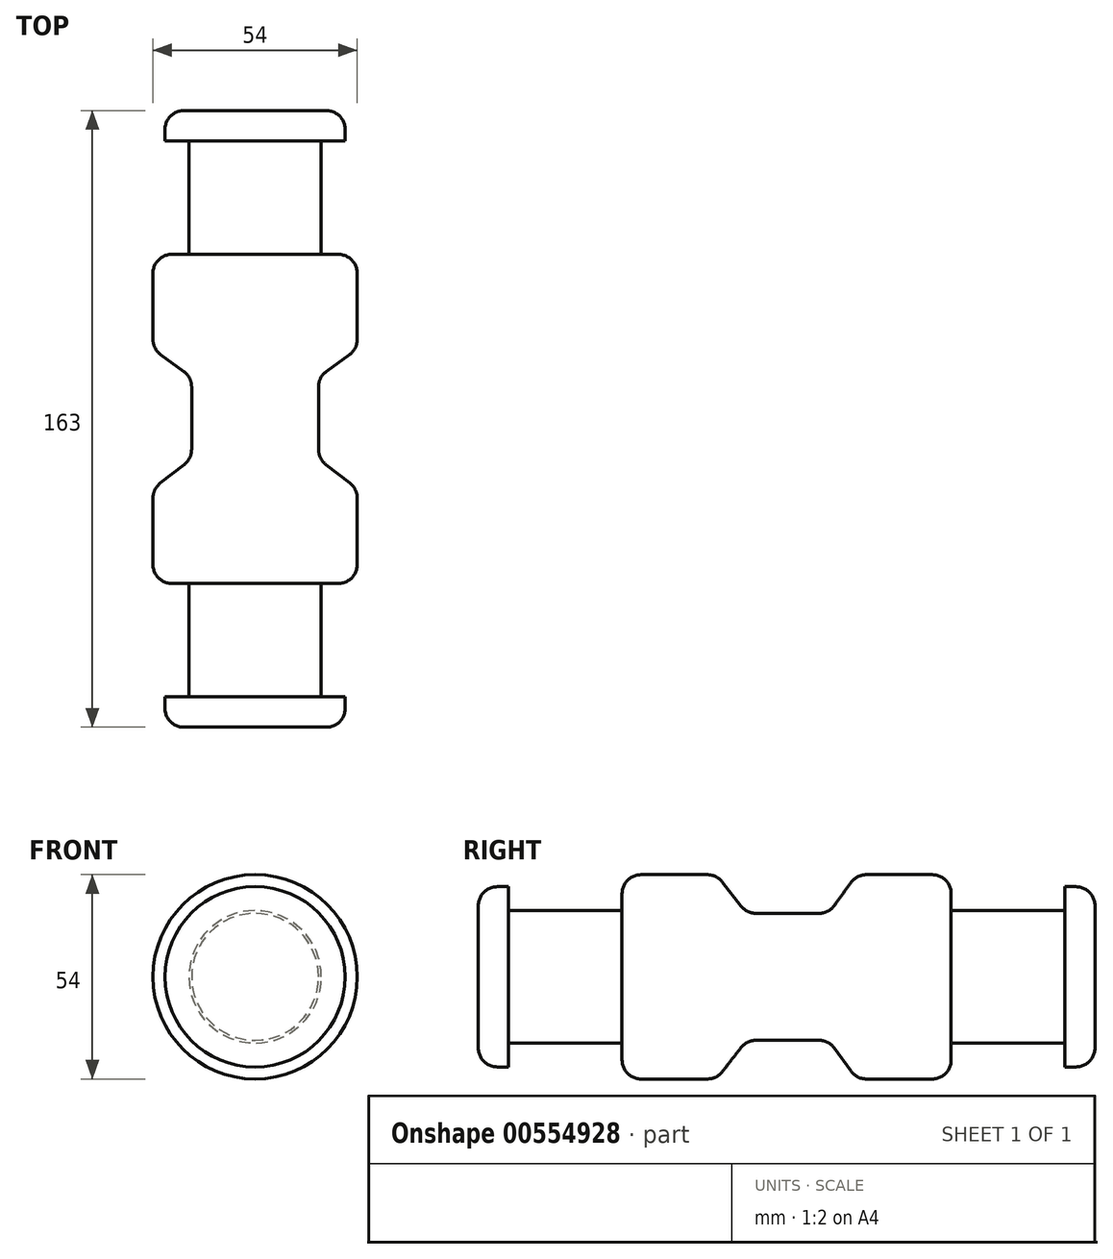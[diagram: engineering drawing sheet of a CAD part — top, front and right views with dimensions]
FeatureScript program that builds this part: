
annotation { "Feature Type Name" : "Feature", "Feature Type Description" : "" }
export const myFeature = defineFeature(function(context is Context, id is Id, definition is map)
    precondition{}
    {
        {
            var Q0;
            Q0=qCreatedBy(makeId("Right.planeOp"),FACE);
            var sketch = newSketch(context, id + "F0", { "sketchPlane" : qUnion([Q0])});
            skLineSegment(sketch, "E0", {"start": v(-81.76, 0) * mm, "end": v(-81.76, 23.82) * mm});
            skLineSegment(sketch, "E1", {"start": v(-81.76, 23.82) * mm, "end": v(-73.76, 23.82) * mm});
            skLineSegment(sketch, "E2", {"start": v(-73.76, 23.82) * mm, "end": v(-73.76, 17.5) * mm});
            skLineSegment(sketch, "E3", {"start": v(-73.76, 17.5) * mm, "end": v(-43.76, 17.5) * mm});
            skLineSegment(sketch, "E4", {"start": v(-43.76, 17.5) * mm, "end": v(-43.76, 27) * mm});
            skLineSegment(sketch, "E5", {"start": v(-43.76, 27) * mm, "end": v(-18.76, 27) * mm});
            skLineSegment(sketch, "E6", {"start": v(43.24, 27) * mm, "end": v(43.24, 17.5) * mm});
            skLineSegment(sketch, "E7", {"start": v(43.24, 17.5) * mm, "end": v(73.24, 17.5) * mm});
            skLineSegment(sketch, "E8", {"start": v(73.24, 17.5) * mm, "end": v(73.24, 23.82) * mm});
            skLineSegment(sketch, "E9", {"start": v(73.24, 23.82) * mm, "end": v(81.24, 23.82) * mm});
            skLineSegment(sketch, "E10", {"start": v(81.24, 23.82) * mm, "end": v(81.24, 0) * mm});
            skLineSegment(sketch, "E11", {"start": v(18.24, 27) * mm, "end": v(10.82, 16.78) * mm});
            skLineSegment(sketch, "E12", {"start": v(10.82, 16.78) * mm, "end": v(-10.81, 16.78) * mm});
            skLineSegment(sketch, "E13", {"start": v(-10.81, 16.78) * mm, "end": v(-18.76, 27) * mm});
            skLineSegment(sketch, "E14.trimOffspring", {"start": v(18.24, 27) * mm, "end": v(43.24, 27) * mm});
            skLineSegment(sketch, "E15", {"start": v(-81.76, 0) * mm, "end": v(81.24, 0) * mm});
            skSolve(sketch);
        }
        {
            var Q0;
            Q0=makeQuery(id+"F0.imprint","IMPRINT",FACE,{"disambiguationData":[TD([[makeQuery(id+"F0.imprint","IMPRINT",EDGE,{"derivedFrom":sQuery(id+"F0.wireOp",EDGE,"E0")}),-1.0]])]});
            var Q1;
            Q1=sQuery(id+"F0.wireOp",EDGE,"E15");
            revolve(context, id + "F1", {"entities" : qUnion([Q0]), "axis" : qUnion([Q1]), "revolveType" : RevolveType.FULL});
        }
        {
            var Q0;
            Q0=makeQuery(id+"F1.opRevolve","SWEPT_EDGE",EDGE,{"disambiguationData":[OSD([sQuery(id+"F0.wireOp",EDGE,"E0"),sQuery(id+"F0.wireOp",EDGE,"E1")])]});
            var Q1;
            Q1=makeQuery(id+"F1.opRevolve","SWEPT_EDGE",EDGE,{"disambiguationData":[OSD([sQuery(id+"F0.wireOp",EDGE,"E4"),sQuery(id+"F0.wireOp",EDGE,"E5")])]});
            var Q2;
            Q2=makeQuery(id+"F1.opRevolve","SWEPT_EDGE",EDGE,{"disambiguationData":[OSD([sQuery(id+"F0.wireOp",EDGE,"E5"),sQuery(id+"F0.wireOp",EDGE,"E13")])]});
            var Q3;
            Q3=makeQuery(id+"F1.opRevolve","SWEPT_EDGE",EDGE,{"disambiguationData":[OSD([sQuery(id+"F0.wireOp",EDGE,"E12"),sQuery(id+"F0.wireOp",EDGE,"E13")])]});
            var Q4;
            Q4=makeQuery(id+"F1.opRevolve","SWEPT_EDGE",EDGE,{"disambiguationData":[OSD([sQuery(id+"F0.wireOp",EDGE,"E11"),sQuery(id+"F0.wireOp",EDGE,"E12")])]});
            var Q5;
            Q5=makeQuery(id+"F1.opRevolve","SWEPT_EDGE",EDGE,{"disambiguationData":[OSD([sQuery(id+"F0.wireOp",EDGE,"E11"),sQuery(id+"F0.wireOp",EDGE,"E14.trimOffspring")])]});
            var Q6;
            Q6=makeQuery(id+"F1.opRevolve","SWEPT_EDGE",EDGE,{"disambiguationData":[OSD([sQuery(id+"F0.wireOp",EDGE,"E6"),sQuery(id+"F0.wireOp",EDGE,"E14.trimOffspring")])]});
            var Q7;
            Q7=makeQuery(id+"F1.opRevolve","SWEPT_EDGE",EDGE,{"disambiguationData":[OSD([sQuery(id+"F0.wireOp",EDGE,"E9"),sQuery(id+"F0.wireOp",EDGE,"E10")])]});
            fillet(context, id + "F2", {"entities" : qUnion([Q0, Q1, Q2, Q3, Q4, Q5, Q6, Q7]), "radius" : 5 * mm, "tangentPropagation" : true, "allowEdgeOverflow" : false});
        }
    });
